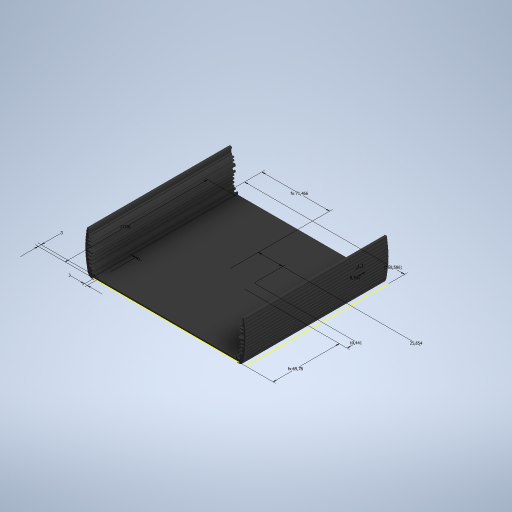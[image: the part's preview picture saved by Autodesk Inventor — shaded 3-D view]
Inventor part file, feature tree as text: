
AUTODESK INVENTOR PART (.ipt)
format: ipt  version: 2024 (Build 280153000, 153)  size: 574,464 bytes
history: native  units: mm
features: other x5, sketch x1, reference x1
ambient origin geometry x8: Origin, YZ Plane, XZ Plane, XY Plane, X Axis, Y Axis, Z Axis, Center Point
bodies: Solid1 (feature_tree), Volumenkörper1 (feature_tree)
feature tree (7):
  sketch  "Sketch1"  dims[d0=0.0mm d1=3.0mm d2=3.0mm d3=10.440924mm d4=69.779538mm d5=150.0mm d6=25.654376mm d7=168.586321mm d8=71.465973mm d9=8.540917mm d10=1.3mm]
  reference  "Reference1"
  other  "<userpath>\Documents\GitHub\REACH-Hardware\CAD\InventorProject\Main_Assembly_GBit.iam"
  other  "Main_Assembly_GBit.iam"
  other  "Front_Panel_Assembly_10Gbit:1"
  other  "Front_Pane_Basel_Assembly:1"
  other  "DI 1600-6000:1"
